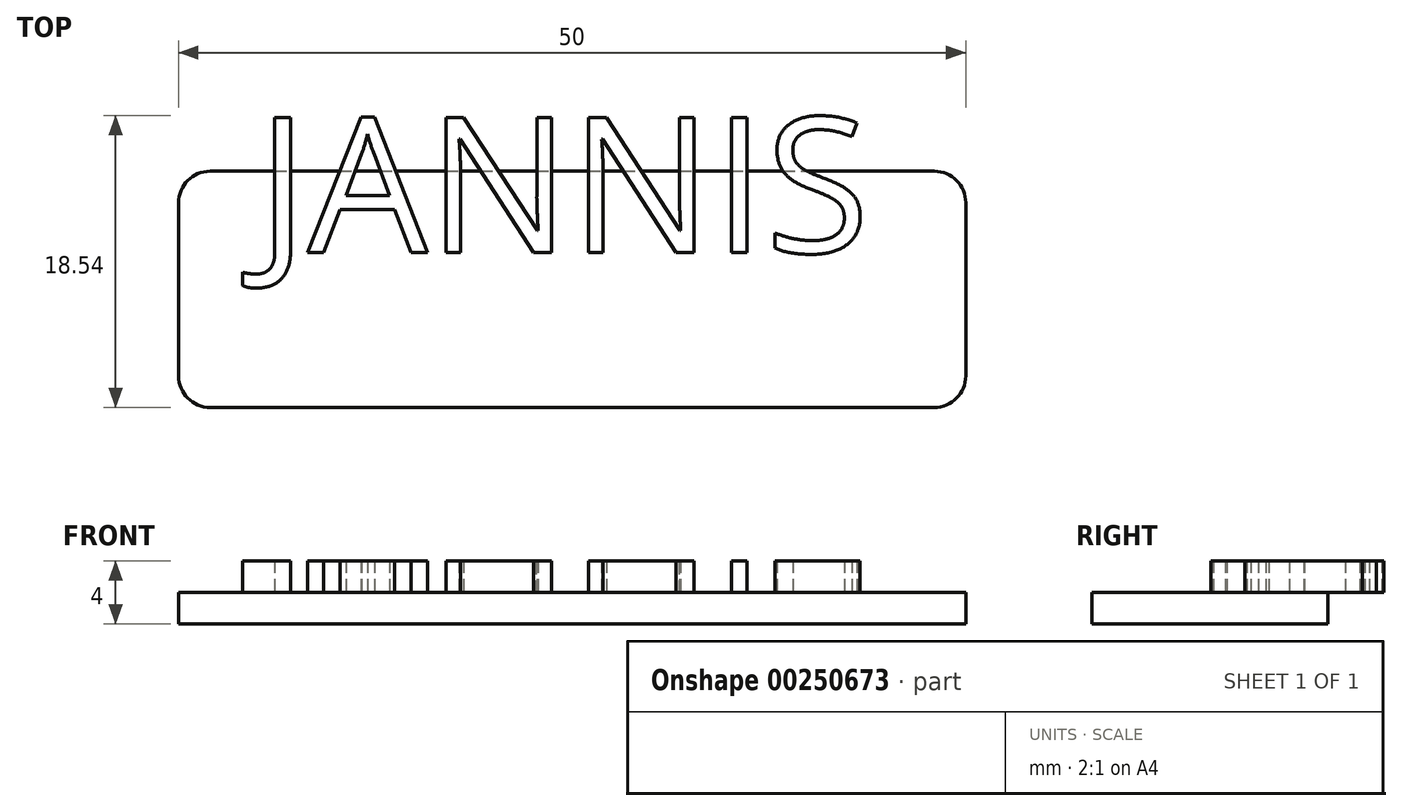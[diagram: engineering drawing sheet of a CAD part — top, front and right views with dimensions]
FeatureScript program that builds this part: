
annotation { "Feature Type Name" : "Feature", "Feature Type Description" : "" }
export const myFeature = defineFeature(function(context is Context, id is Id, definition is map)
    precondition{}
    {
        {
            var Q0;
            Q0=qCreatedBy(makeId("Top.planeOp"),FACE);
            var sketch = newSketch(context, id + "F0", { "sketchPlane" : qUnion([Q0])});
            skLineSegment(sketch, "E0.bottom", {"start": v(-20.43, 1.12) * mm, "end": v(29.57, 1.12) * mm});
            skLineSegment(sketch, "E0.top", {"start": v(-20.43, -13.88) * mm, "end": v(29.57, -13.88) * mm});
            skLineSegment(sketch, "E0.left", {"start": v(-20.43, 1.12) * mm, "end": v(-20.43, -13.88) * mm});
            skLineSegment(sketch, "E0.right", {"start": v(29.57, 1.12) * mm, "end": v(29.57, -13.88) * mm});
            skSolve(sketch);
        }
        {
            var Q0;
            Q0 = qSketchRegion(id + "F0", true);
            extrude(context, id + "F1", {"entities" : qUnion([Q0]), "depth" : 2 * mm});
        }
        {
            var Q0;
            Q0=makeQuery(id+"F1.opExtrude","CAP_FACE",FACE,{"disambiguationData":[OSD([sQuery(id+"F0.wireOp",EDGE,"E0.bottom"),sQuery(id+"F0.wireOp",EDGE,"E0.top"),sQuery(id+"F0.wireOp",EDGE,"E0.left"),sQuery(id+"F0.wireOp",EDGE,"E0.right")])],"isStart":false});
            var sketch = newSketch(context, id + "F2", { "sketchPlane" : qUnion([Q0])});
            skText(sketch, "E1", { "text": "JANNIS", "fontName": "OpenSans-Regular.ttf"});
            skPoint(sketch, "E2", {"position": v(-20.43, -6.38) * mm});
            skPoint(sketch, "E3", {"position": v(29.57, -6.38) * mm});
            skPoint(sketch, "E4", {"position": v(-15.43, -6.38) * mm});
            skPoint(sketch, "E5", {"position": v(24.57, -6.38) * mm});
            skPoint(sketch, "E6", {"position": v(4.57, 1.12) * mm});
            skPoint(sketch, "E7", {"position": v(4.57, -13.88) * mm});
            const initialGuessF2  = {"E1": [-0.01543, -0.00404, 1, 0, 0.00865]};
            skSetInitialGuess(sketch, initialGuessF2);
            skSolve(sketch);
        }
        {
            var Q0;
            Q0 = qSketchRegion(id + "F2", true);
            extrude(context, id + "F3", {"entities" : qUnion([Q0]), "operationType" : NewBodyOperationType.ADD, "depth" : 2 * mm});
        }
        {
            var Q0;
            Q0=makeQuery(id+"F1.opExtrude","SWEPT_EDGE",EDGE,{"disambiguationData":[OSD([sQuery(id+"F0.wireOp",EDGE,"E0.top"),sQuery(id+"F0.wireOp",EDGE,"E0.left")])]});
            var Q1;
            Q1=makeQuery(id+"F1.opExtrude","SWEPT_EDGE",EDGE,{"disambiguationData":[OSD([sQuery(id+"F0.wireOp",EDGE,"E0.bottom"),sQuery(id+"F0.wireOp",EDGE,"E0.left")])]});
            var Q2;
            Q2=makeQuery(id+"F1.opExtrude","SWEPT_EDGE",EDGE,{"disambiguationData":[OSD([sQuery(id+"F0.wireOp",EDGE,"E0.top"),sQuery(id+"F0.wireOp",EDGE,"E0.right")])]});
            var Q3;
            Q3=makeQuery(id+"F1.opExtrude","SWEPT_EDGE",EDGE,{"disambiguationData":[OSD([sQuery(id+"F0.wireOp",EDGE,"E0.bottom"),sQuery(id+"F0.wireOp",EDGE,"E0.right")])]});
            fillet(context, id + "F4", {"entities" : qUnion([Q0, Q1, Q2, Q3]), "radius" : 2 * mm, "tangentPropagation" : true, "allowEdgeOverflow" : false});
        }
    });
